# Revit family: Domotics-DomesticRanges-GEWISS-SYSTEM_COMMAND-TWO-WAY_SWITCH_KEY
name_source: partatom
category: Apparecchi elettrici
revit_build: Autodesk Revit 2016 (Build: 20161004_0715(x64)
units: mm (PartAtom-declared; Revit-internal decimal feet)

## family parameters
Condiviso = Sì
Host = Superficie
Mantenere orientamento annotazione = Sì
Numero OmniClass = 23.80.50.11.14
Punto di calcolo locali = Sì
Quota connettore circolare = Usa diametro
Taglio con vuoti quando caricato = No
Tipo di parte = Normale
Titolo OmniClass = Switches

## types (2) — shared parameters
Button key = With key
Carico apparente = 0 VA
Catalogue = DOMOTICS
Catalogue Range = SYSTEM - DOMESTIC RANGE
Description. = Two-way switch
Description: = 1P - 10AX
Electrocod = 0130
IDF = 7facbd68-6e22-42a1-81bd-1ebbbeee2841
IDT = 9339aafb-4b4f-4cd3-b297-a53a2e736352
Immagine tipo = GW21008.jpg
N. poli = 1
No. SYSTEM modules = 1
Produttore = GEWISS S.p.A.
Prospetto di default = 1219 mm
Pulsante = GEWISS NERO
SEO = 2 way switch
Simbolo = SIMBOLO DEVIATORI : DEVCHIAVE
Technical sheet = https://www.gewiss.com
Type = With key
URL = https://www.gewiss.com
Version file RFA = 19.4
Volt = 230 V
Voltage = 250 V ac
Voltage: = 250 V ac

## per-type parameters (varying)
| type | Colour | Descrizione | EAN code | Modello |
| GW21008 - Key-op.1P 10A 230V 2-way switch black | Black | KEY-OP.1P 10A 230V 2-WAY SWITCH SY/BK | 8011564128026 | GW21008 |
| GW20008 - Key-op.1P 10A 230V 2-way switch white | White | KEY-OP.1P 10A 230V 2-WAY SWITCH SY/WT | 8011564000094 | GW20008 |

## geometry (parser evidence)
native form markers: Sweep x2
no freeform markers — native parametric forms only
